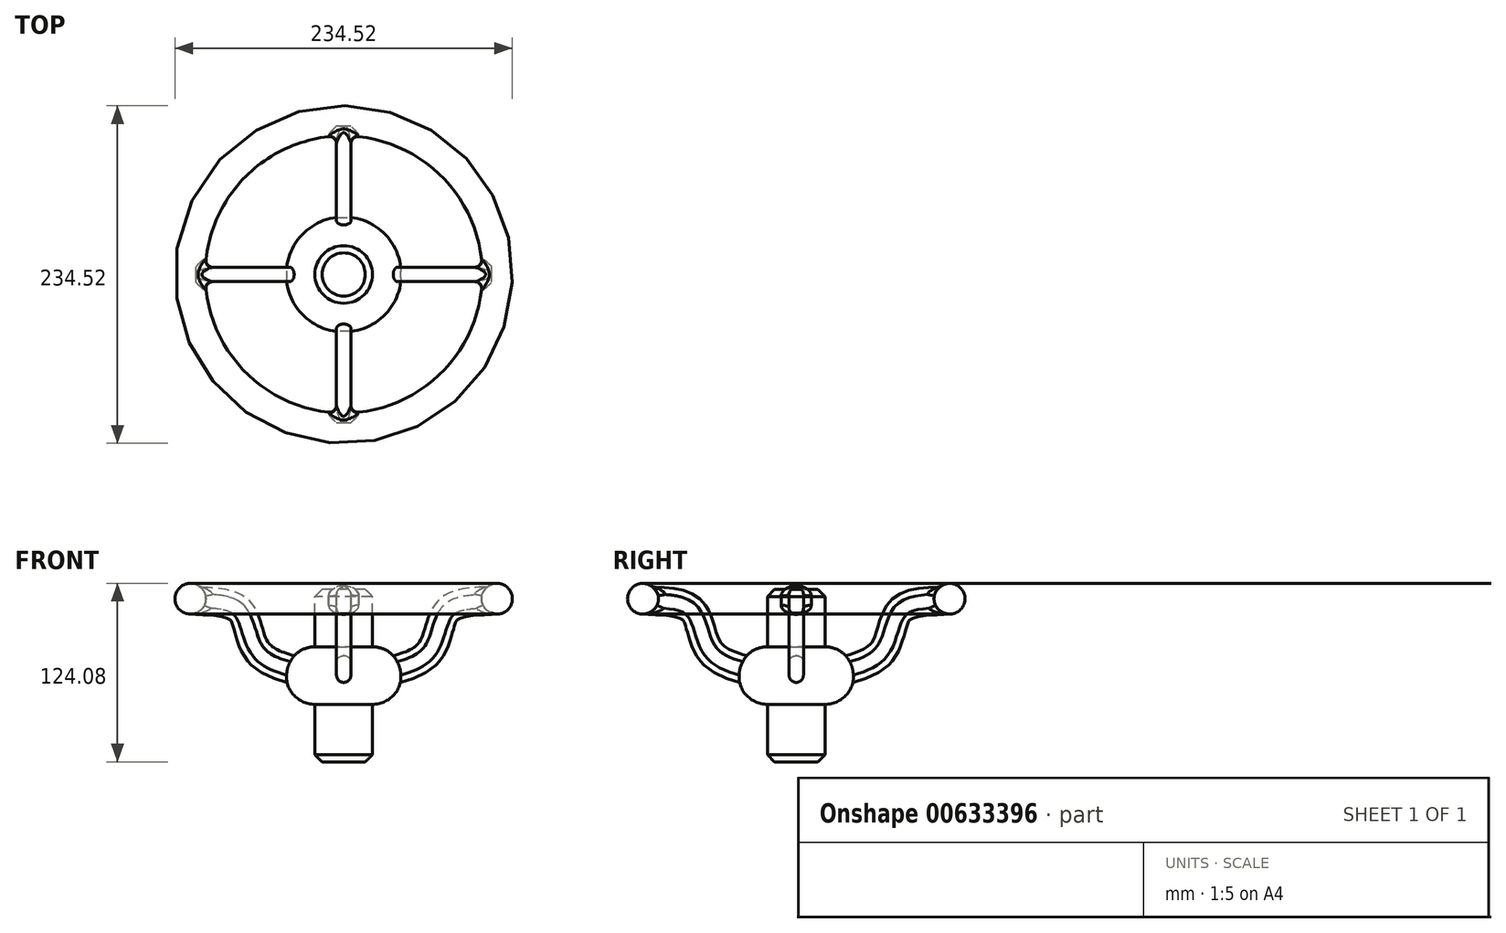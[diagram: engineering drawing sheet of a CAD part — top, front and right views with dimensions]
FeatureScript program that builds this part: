
annotation { "Feature Type Name" : "Feature", "Feature Type Description" : "" }
export const myFeature = defineFeature(function(context is Context, id is Id, definition is map)
    precondition{}
    {
        {
            var Q0;
            Q0=qCreatedBy(makeId("Front.planeOp"),FACE);
            var sketch = newSketch(context, id + "F0", { "sketchPlane" : qUnion([Q0])});
            skLineSegment(sketch, "E0", {"start": v(0, 60) * mm, "end": v(0, -60) * mm});
            skLineSegment(sketch, "E1", {"start": v(0, -60) * mm, "end": v(20, -60) * mm});
            skLineSegment(sketch, "E2", {"start": v(20, -60) * mm, "end": v(20, -20) * mm});
            skLineSegment(sketch, "E3", {"start": v(0, 60) * mm, "end": v(20, 60) * mm});
            skLineSegment(sketch, "E4", {"start": v(20, 60) * mm, "end": v(20, 20) * mm});
            skArc(sketch, "E5", {"start": v(20, -20) * mm, "mid": v(40, 0) * mm, "end": v(20, 20) * mm});
            skSolve(sketch);
        }
        {
            var Q0;
            Q0=makeQuery(id+"F0.imprint","IMPRINT",FACE,{"disambiguationData":[TD([[makeQuery(id+"F0.imprint","IMPRINT",EDGE,{"derivedFrom":sQuery(id+"F0.wireOp",EDGE,"E0")}),1.0]])]});
            var Q1;
            Q1=sQuery(id+"F0.wireOp",EDGE,"E0");
            revolve(context, id + "F1", {"entities" : qUnion([Q0]), "axis" : qUnion([Q1]), "revolveType" : RevolveType.FULL});
        }
        {
            var Q0;
            Q0=makeQuery(id+"F1.opRevolve","SWEPT_EDGE",EDGE,{"disambiguationData":[OSD([sQuery(id+"F0.wireOp",EDGE,"E3"),sQuery(id+"F0.wireOp",EDGE,"E4")])]});
            chamfer(context, id + "F2", {"entities" : qUnion([Q0]), "width" : 5 * mm, "tangentPropagation" : true});
        }
        {
            var Q0;
            Q0=makeQuery(id+"F1.opRevolve","SWEPT_EDGE",EDGE,{"disambiguationData":[OSD([sQuery(id+"F0.wireOp",EDGE,"E1"),sQuery(id+"F0.wireOp",EDGE,"E2")])]});
            chamfer(context, id + "F3", {"entities" : qUnion([Q0]), "width" : 5 * mm, "tangentPropagation" : true});
        }
        {
            var Q0;
            Q0=qCreatedBy(makeId("Front.planeOp"),FACE);
            cPlane(context, id + "F4", {"entities" : qUnion([Q0]), "cplaneType" : CPlaneType.OFFSET, "offset" : 20 * mm, "width" : 150 * mm, "height" : 150 * mm});
        }
        {
            var Q0;
            Q0=qCreatedBy(makeId("Right.planeOp"),FACE);
            cPlane(context, id + "F5", {"entities" : qUnion([Q0]), "cplaneType" : CPlaneType.OFFSET, "offset" : 20 * mm, "width" : 150 * mm, "height" : 150 * mm});
        }
        {
            var Q0;
            Q0=qCreatedBy(id+"F5.planeOp",FACE);
            var sketch = newSketch(context, id + "F6", { "sketchPlane" : qUnion([Q0])});
            skLineSegment(sketch, "E6.bottom", {"start": v(0, -10) * mm, "end": v(0, -10) * mm});
            skLineSegment(sketch, "E6.top", {"start": v(0, 10) * mm, "end": v(0, 10) * mm});
            skLineSegment(sketch, "E6.left", {"start": v(5, -5) * mm, "end": v(5, 5) * mm});
            skLineSegment(sketch, "E6.right", {"start": v(-5, -5) * mm, "end": v(-5, 5) * mm});
            skPoint(sketch, "E6.middle", {"position": v(0, 0) * mm});
            skPoint(sketch, "E7.visualSharp", {"position": v(-5, 10) * mm});
            skArc(sketch, "E7.filletArc", {"start": v(0, 10) * mm, "mid": v(-3.54, 8.54) * mm, "end": v(-5, 5) * mm});
            skPoint(sketch, "E8.visualSharp", {"position": v(5, 10) * mm});
            skArc(sketch, "E8.filletArc", {"start": v(5, 5) * mm, "mid": v(3.54, 8.54) * mm, "end": v(0, 10) * mm});
            skPoint(sketch, "E9.visualSharp", {"position": v(5, -10) * mm});
            skArc(sketch, "E9.filletArc", {"start": v(0, -10) * mm, "mid": v(3.54, -8.54) * mm, "end": v(5, -5) * mm});
            skPoint(sketch, "E10.visualSharp", {"position": v(-5, -10) * mm});
            skArc(sketch, "E10.filletArc", {"start": v(-5, -5) * mm, "mid": v(-3.54, -8.54) * mm, "end": v(0, -10) * mm});
            skSolve(sketch);
        }
        {
            var Q0;
            Q0=qCreatedBy(makeId("Front.planeOp"),FACE);
            var sketch = newSketch(context, id + "F7", { "sketchPlane" : qUnion([Q0])});
            skFitSpline(sketch, "E11", {"points": [v(20.23, 0) * mm, v(50.76, 9.57) * mm, v(63.24, 23.07) * mm, v(73.5, 45.98) * mm, v(105.14, 52.21) * mm], "startDerivative": vector(136.13, 38.5) * mm, "endDerivative": vector(136.18, 7.88) * mm});
            skSolve(sketch);
        }
        {
            var Q0;
            Q0 = qSketchRegion(id + "F6", true);
            var Q1;
            Q1 = qConstructionFilter(qBodyType(qCreatedBy(id + "F7" ,EDGE), BodyType.WIRE), ConstructionObject.NO);
            sweep(context, id + "F8", {"operationType" : NewBodyOperationType.ADD, "profiles" : qUnion([Q0]), "path" : qUnion([Q1])});
        }
        {
            var Q0;
            Q0=makeQuery(id+"F1.opRevolve","SWEPT_BODY",BODY,{"disambiguationData":[OSD([sQuery(id+"F0.wireOp",EDGE,"E0"),sQuery(id+"F0.wireOp",EDGE,"E1"),sQuery(id+"F0.wireOp",EDGE,"E2"),sQuery(id+"F0.wireOp",EDGE,"E3"),sQuery(id+"F0.wireOp",EDGE,"E4"),sQuery(id+"F0.wireOp",EDGE,"E5")])]});
            var Q1;
            Q1=makeQuery(id+"F1.opRevolve","SWEPT_FACE",FACE,{"disambiguationData":[OSD([sQuery(id+"F0.wireOp",EDGE,"E4")])]});
            circularPattern(context, id + "F9", {"entities" : qUnion([Q0]), "axis" : qUnion([Q1]), "angle" : 360 * degree, "instanceCount" : 4, "equalSpace" : true});
        }
        {
            var Q0;
            Q0=qCreatedBy(id+"F4.planeOp",FACE);
            var sketch = newSketch(context, id + "F10", { "sketchPlane" : qUnion([Q0])});
            skCircle(sketch, "E12", {"center": v(104.88, 53.42) * mm, "radius": 10.65 * mm});
            skSolve(sketch);
        }
        {
            var Q0;
            Q0=makeQuery(id+"F10.imprint","IMPRINT",FACE,{"disambiguationData":[TD([[makeQuery(id+"F10.imprint","IMPRINT",EDGE,{"derivedFrom":sQuery(id+"F10.wireOp",EDGE,"E12")}),1.0]])]});
            var Q1;
            Q1=makeQuery(id+"F1.opRevolve","SWEPT_FACE",FACE,{"disambiguationData":[OSD([sQuery(id+"F0.wireOp",EDGE,"E4")])]});
            revolve(context, id + "F11", {"operationType" : NewBodyOperationType.ADD, "entities" : qUnion([Q0]), "axis" : qUnion([Q1]), "revolveType" : RevolveType.FULL});
        }
        {
            var Q0;
            Q0=makeQuery(id+"F11.boolean.opBoolean","INTERSECT",EDGE,{"derivedFrom":[makeQuery(id+"F8.opSweep","SWEPT_FACE",FACE,{"disambiguationData":[OSD([sQuery(id+"F6.wireOp",EDGE,"E7.filletArc"),sQuery(id+"F6.wireOp",EDGE,"E8.filletArc"),sQuery(id+"F7.wireOp",EDGE,"E11")])]}),makeQuery(id+"F11.opRevolve","SWEPT_FACE",FACE,{"disambiguationData":[OSD([sQuery(id+"F10.wireOp",EDGE,"E12")])]})]});
            var Q1;
            Q1=makeQuery(id+"F11.boolean.opBoolean","INTERSECT",EDGE,{"derivedFrom":[makeQuery(id+"F9.opPattern","COPY",FACE,{"derivedFrom":makeQuery(id+"F8.opSweep","SWEPT_FACE",FACE,{"disambiguationData":[OSD([sQuery(id+"F6.wireOp",EDGE,"E7.filletArc"),sQuery(id+"F6.wireOp",EDGE,"E8.filletArc"),sQuery(id+"F7.wireOp",EDGE,"E11")])]}),"instanceName":"1"}),makeQuery(id+"F11.opRevolve","SWEPT_FACE",FACE,{"disambiguationData":[OSD([sQuery(id+"F10.wireOp",EDGE,"E12")])]})]});
            var Q2;
            Q2=makeQuery(id+"F11.boolean.opBoolean","INTERSECT",EDGE,{"derivedFrom":[makeQuery(id+"F9.opPattern","COPY",FACE,{"derivedFrom":makeQuery(id+"F8.opSweep","SWEPT_FACE",FACE,{"disambiguationData":[OSD([sQuery(id+"F6.wireOp",EDGE,"E7.filletArc"),sQuery(id+"F6.wireOp",EDGE,"E8.filletArc"),sQuery(id+"F7.wireOp",EDGE,"E11")])]}),"instanceName":"2"}),makeQuery(id+"F11.opRevolve","SWEPT_FACE",FACE,{"disambiguationData":[OSD([sQuery(id+"F10.wireOp",EDGE,"E12")])]})]});
            var Q3;
            Q3=makeQuery(id+"F11.boolean.opBoolean","INTERSECT",EDGE,{"derivedFrom":[makeQuery(id+"F9.opPattern","COPY",FACE,{"derivedFrom":makeQuery(id+"F8.opSweep","SWEPT_FACE",FACE,{"disambiguationData":[OSD([sQuery(id+"F6.wireOp",EDGE,"E7.filletArc"),sQuery(id+"F6.wireOp",EDGE,"E8.filletArc"),sQuery(id+"F7.wireOp",EDGE,"E11")])]}),"instanceName":"3"}),makeQuery(id+"F11.opRevolve","SWEPT_FACE",FACE,{"disambiguationData":[OSD([sQuery(id+"F10.wireOp",EDGE,"E12")])]})]});
            fillet(context, id + "F12", {"entities" : qUnion([Q0, Q1, Q2, Q3]), "radius" : 5 * mm, "tangentPropagation" : true, "allowEdgeOverflow" : false});
        }
    });
